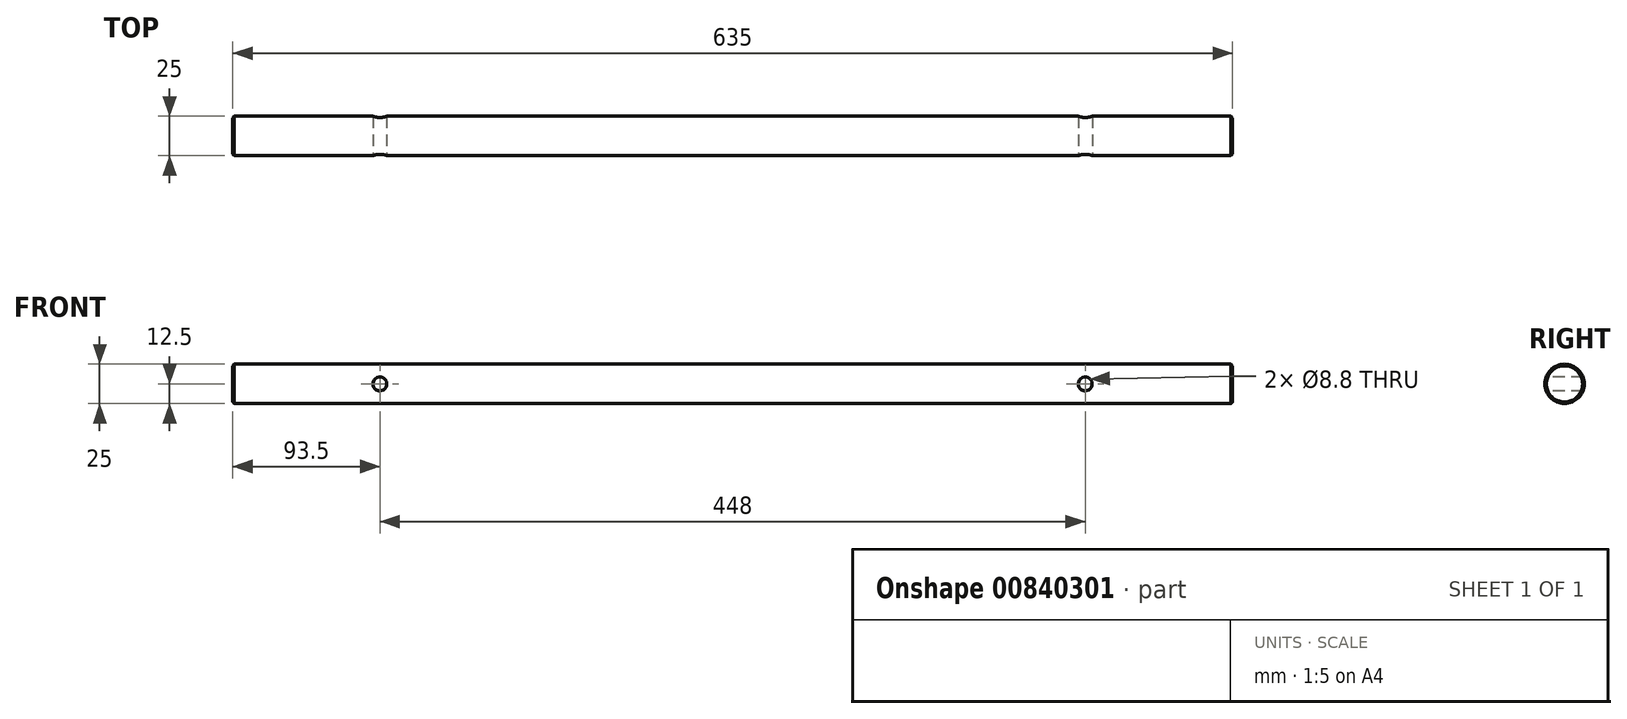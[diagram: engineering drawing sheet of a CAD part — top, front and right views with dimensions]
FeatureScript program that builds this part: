
annotation { "Feature Type Name" : "Feature", "Feature Type Description" : "" }
export const myFeature = defineFeature(function(context is Context, id is Id, definition is map)
    precondition{}
    {
        {
            var Q0;
            Q0=qCreatedBy(makeId("Right.planeOp"),FACE);
            var sketch = newSketch(context, id + "F0", { "sketchPlane" : qUnion([Q0])});
            skCircle(sketch, "E0", {"center": v(0, 0) * mm, "radius": 12.5 * mm});
            skSolve(sketch);
        }
        {
            var Q0;
            Q0=makeQuery(id+"F0.imprint","IMPRINT",FACE,{"disambiguationData":[TD([[makeQuery(id+"F0.imprint","IMPRINT",EDGE,{"derivedFrom":sQuery(id+"F0.wireOp",EDGE,"E0")}),1.0]])]});
            extrude(context, id + "F1", {"entities" : qUnion([Q0]), "endBound" : BoundingType.SYMMETRIC, "depth" : 635 * mm, "offsetDistance" : 25 * mm});
        }
        {
            var Q0;
            Q0=qCreatedBy(makeId("Front.planeOp"),FACE);
            cPlane(context, id + "F2", {"entities" : qUnion([Q0]), "cplaneType" : CPlaneType.OFFSET, "offset" : 25 * mm, "width" : 150 * mm, "height" : 150 * mm});
        }
        {
            var Q0;
            Q0=qCreatedBy(id+"F2.planeOp",FACE);
            var sketch = newSketch(context, id + "F3", { "sketchPlane" : qUnion([Q0])});
            skPoint(sketch, "E1", {"position": v(-224, 0) * mm});
            skPoint(sketch, "E2", {"position": v(224, 0) * mm});
            skSolve(sketch);
        }
        {
            var Q0;
            Q0=sQuery(id+"F3.wireOp",VERTEX,"E1");
            var Q1;
            Q1=sQuery(id+"F3.wireOp",VERTEX,"E2");
            var Q2;
            Q2=makeQuery(id+"F1.opExtrude","SWEPT_BODY",BODY,{"disambiguationData":[OSD([sQuery(id+"F0.wireOp",EDGE,"E0")])]});
            hole(context, id + "F4", {"style" : HoleStyle.SIMPLE, "endStyle" : HoleEndStyle.THROUGH, "standardTappedOrClearance" : lookupTablePath({ "fit" : "Normal", "standard" : "ISO", "size" : "M8", "type" : "Clearance" }), "standardBlindInLast" : lookupTablePath({ "fit" : "Standard", "standard" : "ISO", "size" : "M8", "type" : "Clearance" }), "holeDiameter" : 8.8 * mm, "majorDiameter" : 5 * mm, "isTappedThrough" : true, "tappedDepth" : 20 * mm, "tapClearance" : 3, "startFromSketch" : true, "locations" : qUnion([Q0, Q1]), "scope" : qUnion([Q2])});
        }
        {
            var Q0;
            Q0=makeQuery(id+"F1.opExtrude","CAP_FACE",FACE,{"disambiguationData":[OSD([sQuery(id+"F0.wireOp",EDGE,"E0")])],"isStart":false});
            var Q1;
            Q1=makeQuery(id+"F1.opExtrude","CAP_FACE",FACE,{"disambiguationData":[OSD([sQuery(id+"F0.wireOp",EDGE,"E0")])],"isStart":true});
            chamfer(context, id + "F5", {"entities" : qUnion([Q0, Q1]), "width" : 1 * mm, "tangentPropagation" : true});
        }
    });
